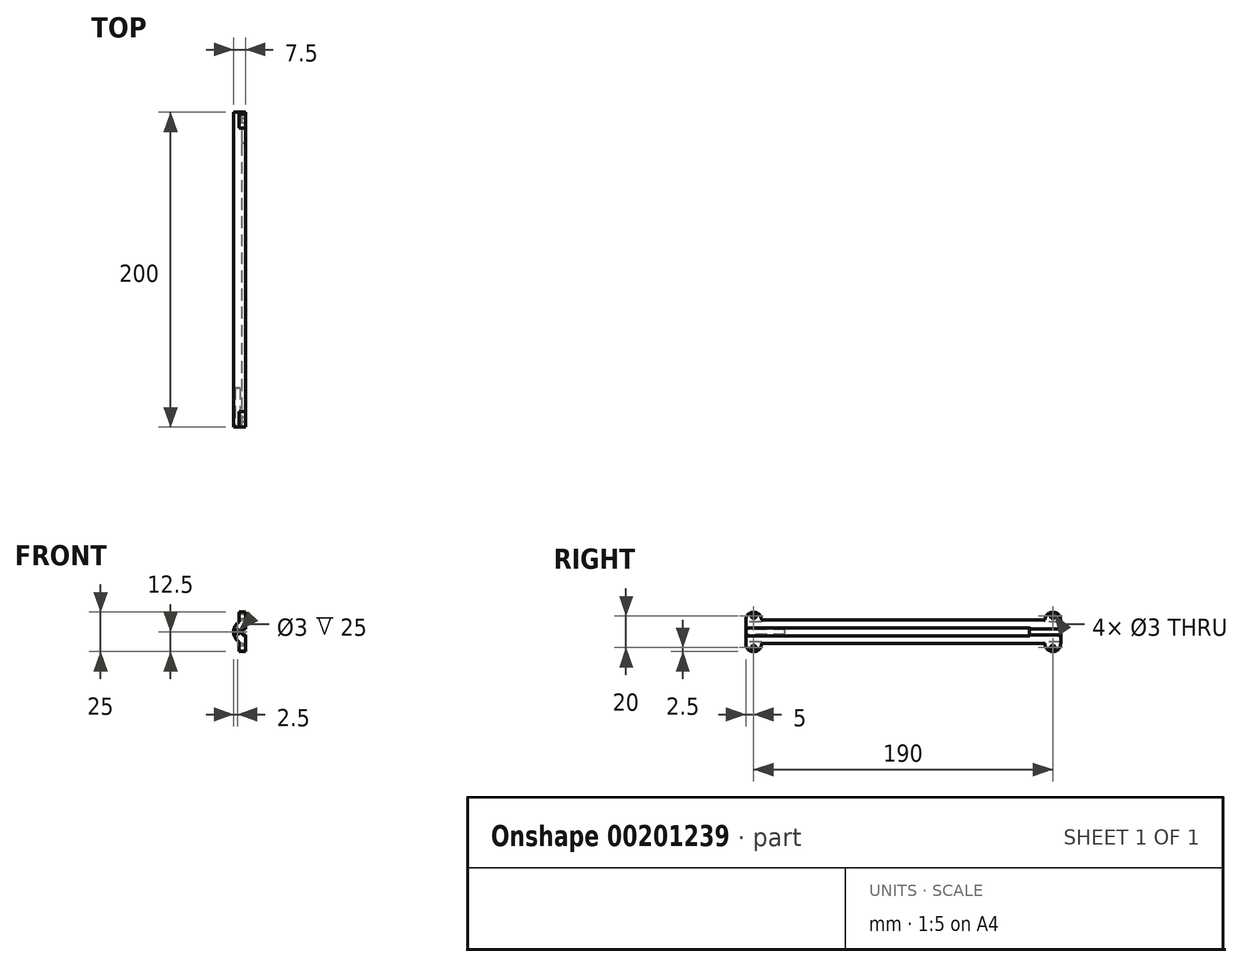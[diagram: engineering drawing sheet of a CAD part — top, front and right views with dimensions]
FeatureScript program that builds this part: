
annotation { "Feature Type Name" : "Feature", "Feature Type Description" : "" }
export const myFeature = defineFeature(function(context is Context, id is Id, definition is map)
    precondition{}
    {
        {
            var Q0;
            Q0=qCreatedBy(makeId("Front.planeOp"),FACE);
            var sketch = newSketch(context, id + "F0", { "sketchPlane" : qUnion([Q0])});
            skCircle(sketch, "E0", {"center": v(0, 0) * mm, "radius": 7.5 * mm});
            skCircle(sketch, "E1", {"center": v(0, 0) * mm, "radius": 2.5 * mm});
            skSolve(sketch);
        }
        {
            var Q0;
            Q0 = qSketchRegion(id + "F0", true);
            extrude(context, id + "F1", {"entities" : qUnion([Q0]), "oppositeDirection" : true, "depth" : 200 * mm});
        }
        {
            var Q0;
            Q0=makeQuery(id+"F1.opExtrude","CAP_FACE",FACE,{"disambiguationData":[OSD([sQuery(id+"F0.wireOp",EDGE,"E0"),sQuery(id+"F0.wireOp",EDGE,"E1")])],"isStart":true});
            var sketch = newSketch(context, id + "F2", { "sketchPlane" : qUnion([Q0])});
            skPoint(sketch, "E2", {"position": v(5, 0) * mm});
            skPoint(sketch, "E3", {"position": v(-5, 0) * mm});
            skCircle(sketch, "E4", {"center": v(5, 0) * mm, "radius": 1.5 * mm});
            skCircle(sketch, "E5", {"center": v(-5, 0) * mm, "radius": 1.5 * mm});
            skSolve(sketch);
        }
        {
            var Q0;
            Q0 = qSketchRegion(id + "F2", true);
            extrude(context, id + "F3", {"entities" : qUnion([Q0]), "operationType" : NewBodyOperationType.REMOVE, "oppositeDirection" : true, "depth" : 25 * mm});
        }
        {
            var Q0;
            Q0=qCreatedBy(makeId("Right.planeOp"),FACE);
            var sketch = newSketch(context, id + "F4", { "sketchPlane" : qUnion([Q0])});
            skLineSegment(sketch, "E6.bottom", {"start": v(0, 16.4) * mm, "end": v(255.63, 16.4) * mm});
            skLineSegment(sketch, "E6.top", {"start": v(0, -18.35) * mm, "end": v(255.63, -18.35) * mm});
            skLineSegment(sketch, "E6.left", {"start": v(0, 16.4) * mm, "end": v(0, -18.35) * mm});
            skLineSegment(sketch, "E6.right", {"start": v(255.63, 16.4) * mm, "end": v(255.63, -18.35) * mm});
            skSolve(sketch);
        }
        {
            var Q0;
            Q0 = qSketchRegion(id + "F4", true);
            extrude(context, id + "F5", {"entities" : qUnion([Q0]), "operationType" : NewBodyOperationType.REMOVE, "depth" : 25 * mm});
        }
        {
            var Q0;
            Q0=makeQuery(id+"F5.boolean.opBoolean","COPY",FACE,{"disambiguationData":[OD(1.0)],"derivedFrom":makeQuery(id+"F5.opExtrude","CAP_FACE",FACE,{"disambiguationData":[OSD([sQuery(id+"F4.wireOp",EDGE,"E6.bottom"),sQuery(id+"F4.wireOp",EDGE,"E6.top"),sQuery(id+"F4.wireOp",EDGE,"E6.left"),sQuery(id+"F4.wireOp",EDGE,"E6.right")])],"isStart":true})});
            var sketch = newSketch(context, id + "F6", { "sketchPlane" : qUnion([Q0])});
            skPoint(sketch, "E7", {"position": v(5, 7.5) * mm});
            skPoint(sketch, "E8", {"position": v(195, 7.5) * mm});
            skArc(sketch, "E9", {"start": v(0, 7.5) * mm, "mid": v(5, 12.5) * mm, "end": v(10, 7.5) * mm});
            skArc(sketch, "E10", {"start": v(200, 7.5) * mm, "mid": v(195, 12.5) * mm, "end": v(190, 7.5) * mm});
            skPoint(sketch, "E11", {"position": v(5, -7.5) * mm});
            skPoint(sketch, "E12", {"position": v(195, -7.5) * mm});
            skArc(sketch, "E13", {"start": v(200, -7.5) * mm, "mid": v(195, -12.5) * mm, "end": v(190, -7.5) * mm});
            skPoint(sketch, "E14", {"position": v(0, -7.5) * mm});
            skPoint(sketch, "E14.positionSnap0", {"position": v(0, 5) * mm});
            skArc(sketch, "E15", {"start": v(0, -7.5) * mm, "mid": v(5, -12.5) * mm, "end": v(10, -7.5) * mm});
            skLineSegment(sketch, "E16.bottom", {"start": v(0, 7.5) * mm, "end": v(10, 7.5) * mm});
            skLineSegment(sketch, "E16.top", {"start": v(0, 2.5) * mm, "end": v(10, 2.5) * mm});
            skLineSegment(sketch, "E16.left", {"start": v(0, 7.5) * mm, "end": v(0, 2.5) * mm});
            skLineSegment(sketch, "E16.right", {"start": v(10, 7.5) * mm, "end": v(10, 2.5) * mm});
            skLineSegment(sketch, "E17.bottom", {"start": v(0, -7.5) * mm, "end": v(10, -7.5) * mm});
            skLineSegment(sketch, "E17.top", {"start": v(0, -2.62) * mm, "end": v(10, -2.62) * mm});
            skLineSegment(sketch, "E17.left", {"start": v(0, -7.5) * mm, "end": v(0, -2.62) * mm});
            skLineSegment(sketch, "E17.right", {"start": v(10, -7.5) * mm, "end": v(10, -2.62) * mm});
            skLineSegment(sketch, "E18.bottom", {"start": v(200, -7.5) * mm, "end": v(190, -7.5) * mm});
            skLineSegment(sketch, "E18.top", {"start": v(200, -2.62) * mm, "end": v(190, -2.62) * mm});
            skLineSegment(sketch, "E18.left", {"start": v(200, -7.5) * mm, "end": v(200, -2.62) * mm});
            skLineSegment(sketch, "E18.right", {"start": v(190, -7.5) * mm, "end": v(190, -2.62) * mm});
            skLineSegment(sketch, "E19.bottom", {"start": v(200, 2.5) * mm, "end": v(190, 2.5) * mm});
            skLineSegment(sketch, "E19.top", {"start": v(200, 7.5) * mm, "end": v(190, 7.5) * mm});
            skLineSegment(sketch, "E19.left", {"start": v(200, 2.5) * mm, "end": v(200, 7.5) * mm});
            skLineSegment(sketch, "E19.right", {"start": v(190, 2.5) * mm, "end": v(190, 7.5) * mm});
            skSolve(sketch);
        }
        {
            var Q0;
            Q0 = qSketchRegion(id + "F6", true);
            extrude(context, id + "F7", {"entities" : qUnion([Q0]), "operationType" : NewBodyOperationType.ADD, "oppositeDirection" : true, "depth" : 4 * mm});
        }
        {
            var Q0;
            Q0=makeQuery(id+"F7.boolean.opBoolean","MERGE",FACE,{"derivedFrom":[makeQuery(id+"F5.boolean.opBoolean","COPY",FACE,{"disambiguationData":[OD(1.0)],"derivedFrom":makeQuery(id+"F5.opExtrude","CAP_FACE",FACE,{"disambiguationData":[OSD([sQuery(id+"F4.wireOp",EDGE,"E6.bottom"),sQuery(id+"F4.wireOp",EDGE,"E6.top"),sQuery(id+"F4.wireOp",EDGE,"E6.left"),sQuery(id+"F4.wireOp",EDGE,"E6.right")])],"isStart":true})}),makeQuery(id+"F7.opExtrude","CAP_FACE",FACE,{"disambiguationData":[OSD([sQuery(id+"F6.wireOp",EDGE,"E9"),sQuery(id+"F6.wireOp",EDGE,"E16.top"),sQuery(id+"F6.wireOp",EDGE,"E16.left"),sQuery(id+"F6.wireOp",EDGE,"E16.right")])],"isStart":true}),makeQuery(id+"F7.opExtrude","CAP_FACE",FACE,{"disambiguationData":[OSD([sQuery(id+"F6.wireOp",EDGE,"E10"),sQuery(id+"F6.wireOp",EDGE,"E19.bottom"),sQuery(id+"F6.wireOp",EDGE,"E19.left"),sQuery(id+"F6.wireOp",EDGE,"E19.right")])],"isStart":true})]});
            var sketch = newSketch(context, id + "F8", { "sketchPlane" : qUnion([Q0])});
            skPoint(sketch, "E20", {"position": v(5, 7.5) * mm});
            skPoint(sketch, "E21", {"position": v(195, 7.5) * mm});
            skPoint(sketch, "E22", {"position": v(5, -10) * mm});
            skPoint(sketch, "E23", {"position": v(195, -10) * mm});
            skPoint(sketch, "E24", {"position": v(5, 10) * mm});
            skPoint(sketch, "E25", {"position": v(195, 10) * mm});
            skPoint(sketch, "E26", {"position": v(5, 0) * mm});
            skPoint(sketch, "E27", {"position": v(195, 0) * mm});
            skCircle(sketch, "E28", {"center": v(5, 10) * mm, "radius": 1.5 * mm});
            skCircle(sketch, "E29", {"center": v(5, -10) * mm, "radius": 1.5 * mm});
            skCircle(sketch, "E30", {"center": v(195, 10) * mm, "radius": 1.5 * mm});
            skCircle(sketch, "E31", {"center": v(195, -10) * mm, "radius": 1.5 * mm});
            skSolve(sketch);
        }
        {
            var Q0;
            Q0 = qSketchRegion(id + "F8", true);
            extrude(context, id + "F9", {"entities" : qUnion([Q0]), "operationType" : NewBodyOperationType.REMOVE, "endBound" : BoundingType.THROUGH_ALL, "oppositeDirection" : true, "depth" : 25 * mm});
        }
        {
            var Q0;
            Q0=makeQuery(id+"F7.boolean.opBoolean","MERGE",FACE,{"derivedFrom":[makeQuery(id+"F1.opExtrude","CAP_FACE",FACE,{"disambiguationData":[OSD([sQuery(id+"F0.wireOp",EDGE,"E0"),sQuery(id+"F0.wireOp",EDGE,"E1")])],"isStart":false}),makeQuery(id+"F7.opExtrude","SWEPT_FACE",FACE,{"disambiguationData":[OSD([sQuery(id+"F6.wireOp",EDGE,"E18.left")])]}),makeQuery(id+"F7.opExtrude","SWEPT_FACE",FACE,{"disambiguationData":[OSD([sQuery(id+"F6.wireOp",EDGE,"E19.left")])]})]});
            var sketch = newSketch(context, id + "F10", { "sketchPlane" : qUnion([Q0])});
            skPoint(sketch, "E32", {"position": v(0, 0) * mm});
            skArc(sketch, "E33", {"start": v(0, -2) * mm, "mid": v(2, 0) * mm, "end": v(0, 2) * mm});
            skLineSegment(sketch, "E34", {"start": v(0, 2) * mm, "end": v(0, -2) * mm});
            skArc(sketch, "E35", {"start": v(0, -2.5) * mm, "mid": v(2.5, 0) * mm, "end": v(0, 2.5) * mm});
            skLineSegment(sketch, "E36", {"start": v(0, 2.5) * mm, "end": v(0, 2) * mm});
            skLineSegment(sketch, "E37", {"start": v(0, -2) * mm, "end": v(0, -2.5) * mm});
            skSolve(sketch);
        }
        {
            var Q0;
            Q0=makeQuery(id+"F10.imprint","IMPRINT",FACE,{"disambiguationData":[TD([[makeQuery(id+"F10.imprint","IMPRINT",EDGE,{"derivedFrom":sQuery(id+"F10.wireOp",EDGE,"E33")}),-1.0]])]});
            extrude(context, id + "F11", {"entities" : qUnion([Q0]), "operationType" : NewBodyOperationType.ADD, "oppositeDirection" : true, "depth" : 20 * mm});
        }
        {
            var Q0;
            Q0=makeQuery(id+"F11.opExtrude","CAP_EDGE",EDGE,{"disambiguationData":[OSD([sQuery(id+"F10.wireOp",EDGE,"E33")])],"isStart":false});
            var Q1;
            Q1=makeQuery(id+"F11.opExtrude","CAP_EDGE",EDGE,{"disambiguationData":[OSD([sQuery(id+"F10.wireOp",EDGE,"E33")])],"isStart":true});
            fillet(context, id + "F12", {"entities" : qUnion([Q0, Q1]), "radius" : 2 * mm, "tangentPropagation" : true, "allowEdgeOverflow" : false});
        }
    });
